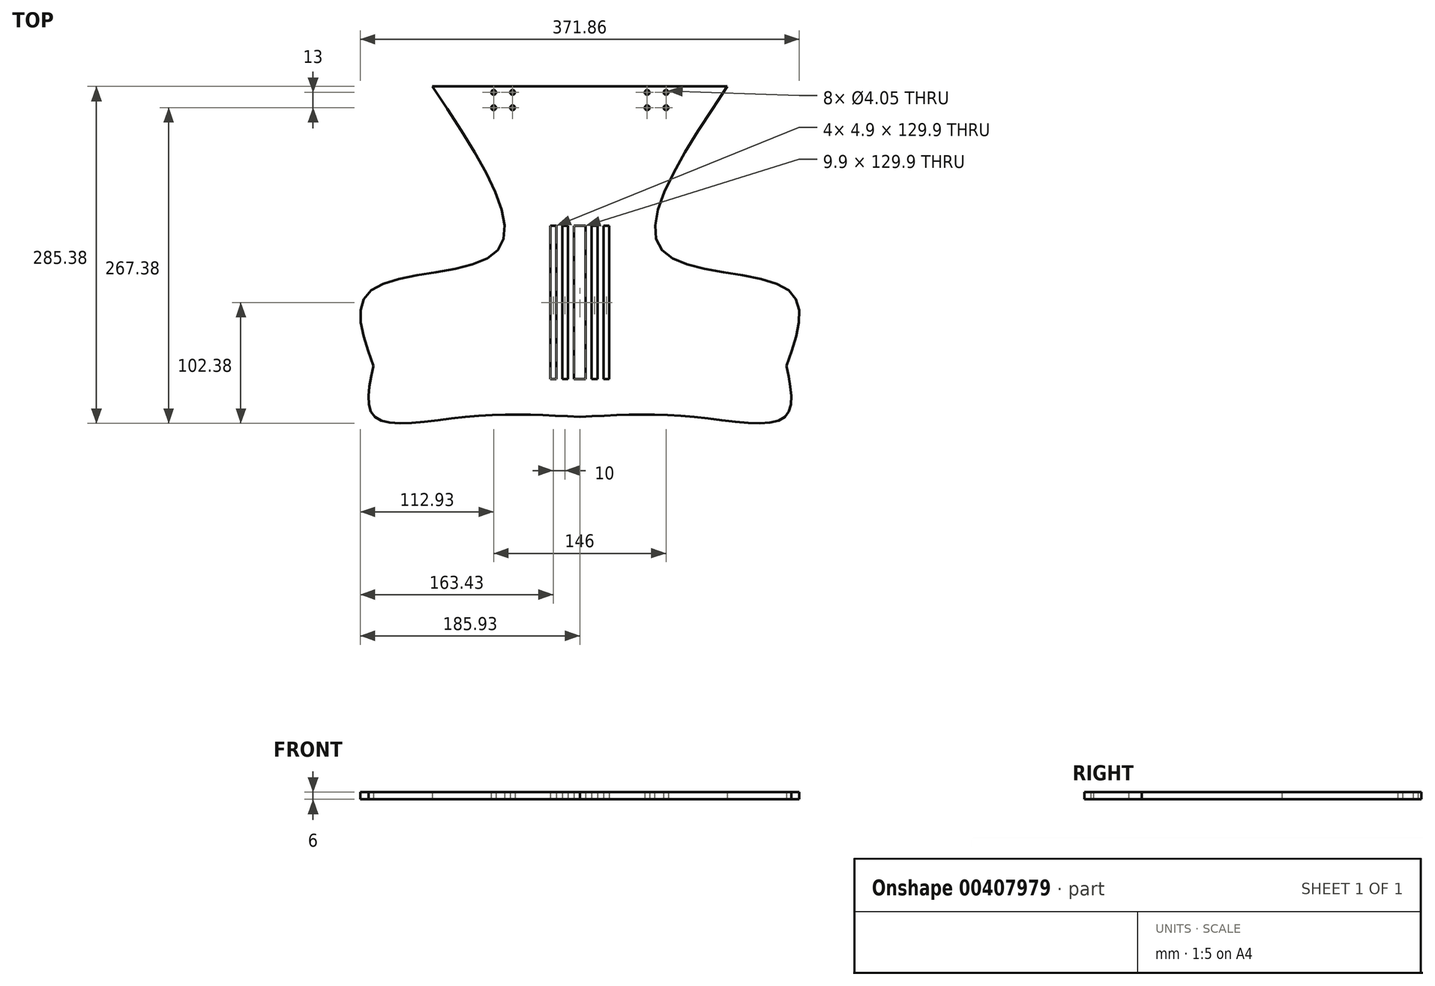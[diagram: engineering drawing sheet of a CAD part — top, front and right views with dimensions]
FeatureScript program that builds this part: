
annotation { "Feature Type Name" : "Feature", "Feature Type Description" : "" }
export const myFeature = defineFeature(function(context is Context, id is Id, definition is map)
    precondition{}
    {
        {
            var Q0;
            Q0=qCreatedBy(makeId("Top.planeOp"),FACE);
            var sketch = newSketch(context, id + "F0", { "sketchPlane" : qUnion([Q0])});
            skLineSegment(sketch, "E0.bottom", {"start": v(-125, 0) * mm, "end": v(125, 0) * mm, "construction": true});
            skLineSegment(sketch, "E0.top", {"start": v(-125, -280) * mm, "end": v(125, -280) * mm, "construction": true});
            skLineSegment(sketch, "E0.left", {"start": v(-125, 0) * mm, "end": v(-125, -280) * mm, "construction": true});
            skLineSegment(sketch, "E0.right", {"start": v(125, 0) * mm, "end": v(125, -280) * mm, "construction": true});
            skFitSpline(sketch, "E1", {"points": [v(-125, 0) * mm, v(-175, -236.88) * mm], "startDerivative": vector(163.58, -419.06) * mm, "endDerivative": vector(5.98, -192.46) * mm});
            skPoint(sketch, "E2", {"position": v(0, -280) * mm});
            skFitSpline(sketch, "E3", {"points": [v(-175, -236.88) * mm, v(0, -280) * mm], "startDerivative": vector(4.02, -129.37) * mm, "endDerivative": vector(290.73, 0) * mm});
            skFitSpline(sketch, "E4.MirrorCS", {"points": [v(125, 0) * mm, v(175, -236.88) * mm], "startDerivative": vector(-163.58, -419.06) * mm, "endDerivative": vector(-5.98, -192.46) * mm});
            skFitSpline(sketch, "E5.MirrorCS", {"points": [v(175, -236.88) * mm, v(0, -280) * mm], "startDerivative": vector(-4.02, -129.37) * mm, "endDerivative": vector(-290.73, 0) * mm});
            skFitSpline(sketch, "E6", {"points": [v(-125, 0) * mm, v(0, 25) * mm], "startDerivative": vector(-31, 79.42) * mm, "endDerivative": vector(148.36, 0.98) * mm});
            skFitSpline(sketch, "E7.MirrorCS", {"points": [v(125, 0) * mm, v(0, 25) * mm], "startDerivative": vector(31, 79.42) * mm, "endDerivative": vector(-148.36, 0.98) * mm});
            skLineSegment(sketch, "E8.bottom", {"start": v(-10, -88) * mm, "end": v(-5, -88) * mm, "construction": true});
            skLineSegment(sketch, "E8.top", {"start": v(-10, -278) * mm, "end": v(-5, -278) * mm, "construction": true});
            skLineSegment(sketch, "E8.left", {"start": v(-10, -88) * mm, "end": v(-10, -278) * mm, "construction": true});
            skLineSegment(sketch, "E8.right", {"start": v(-5, -88) * mm, "end": v(-5, -278) * mm, "construction": true});
            skLineSegment(sketch, "E9.1.0.0", {"start": v(-20, -88) * mm, "end": v(-20, -278) * mm, "construction": true});
            skLineSegment(sketch, "E9.1.0.1", {"start": v(-15, -88) * mm, "end": v(-15, -278) * mm, "construction": true});
            skLineSegment(sketch, "E9.1.0.2", {"start": v(-20, -88) * mm, "end": v(-15, -88) * mm, "construction": true});
            skLineSegment(sketch, "E9.1.0.3", {"start": v(-20, -278) * mm, "end": v(-15, -278) * mm, "construction": true});
            skLineSegment(sketch, "E9.2.0.0", {"start": v(-30, -88) * mm, "end": v(-30, -278) * mm, "construction": true});
            skLineSegment(sketch, "E9.2.0.1", {"start": v(-25, -88) * mm, "end": v(-25, -278) * mm, "construction": true});
            skLineSegment(sketch, "E9.2.0.2", {"start": v(-30, -88) * mm, "end": v(-25, -88) * mm, "construction": true});
            skLineSegment(sketch, "E9.2.0.3", {"start": v(-30, -278) * mm, "end": v(-25, -278) * mm, "construction": true});
            skLineSegment(sketch, "E9.direction1", {"start": v(-10, -278) * mm, "end": v(-20, -278) * mm, "construction": true});
            skLineSegment(sketch, "E10.MirrorCS", {"start": v(10, -278) * mm, "end": v(20, -278) * mm, "construction": true});
            skLineSegment(sketch, "E11.MirrorCS", {"start": v(20, -278) * mm, "end": v(15, -278) * mm, "construction": true});
            skLineSegment(sketch, "E12.MirrorCS", {"start": v(10, -278) * mm, "end": v(5, -278) * mm, "construction": true});
            skLineSegment(sketch, "E13.MirrorCS", {"start": v(20, -88) * mm, "end": v(15, -88) * mm, "construction": true});
            skLineSegment(sketch, "E14.MirrorCS", {"start": v(30, -278) * mm, "end": v(25, -278) * mm, "construction": true});
            skLineSegment(sketch, "E15.MirrorCS", {"start": v(10, -88) * mm, "end": v(5, -88) * mm, "construction": true});
            skLineSegment(sketch, "E16.MirrorCS", {"start": v(30, -88) * mm, "end": v(25, -88) * mm, "construction": true});
            skLineSegment(sketch, "E17.MirrorCS", {"start": v(30, -88) * mm, "end": v(30, -278) * mm, "construction": true});
            skLineSegment(sketch, "E18.MirrorCS", {"start": v(10, -88) * mm, "end": v(10, -278) * mm, "construction": true});
            skLineSegment(sketch, "E19.MirrorCS", {"start": v(15, -88) * mm, "end": v(15, -278) * mm, "construction": true});
            skLineSegment(sketch, "E20.MirrorCS", {"start": v(5, -88) * mm, "end": v(5, -278) * mm, "construction": true});
            skLineSegment(sketch, "E21.MirrorCS", {"start": v(20, -88) * mm, "end": v(20, -278) * mm, "construction": true});
            skLineSegment(sketch, "E22.MirrorCS", {"start": v(25, -88) * mm, "end": v(25, -278) * mm, "construction": true});
            skLineSegment(sketch, "E23.bottom", {"start": v(-73, -5) * mm, "end": v(-57, -5) * mm, "construction": true});
            skLineSegment(sketch, "E23.top", {"start": v(-73, -18) * mm, "end": v(-57, -18) * mm, "construction": true});
            skLineSegment(sketch, "E23.left", {"start": v(-73, -5) * mm, "end": v(-73, -18) * mm, "construction": true});
            skLineSegment(sketch, "E23.right", {"start": v(-57, -5) * mm, "end": v(-57, -18) * mm, "construction": true});
            skCircle(sketch, "E24", {"center": v(-73, -5) * mm, "radius": 2.02 * mm, "construction": true});
            skCircle(sketch, "E25", {"center": v(-57, -5) * mm, "radius": 2.02 * mm, "construction": true});
            skCircle(sketch, "E26", {"center": v(-57, -18) * mm, "radius": 2.02 * mm, "construction": true});
            skCircle(sketch, "E27", {"center": v(-73, -18) * mm, "radius": 2.02 * mm, "construction": true});
            skPoint(sketch, "E28", {"position": v(-65, -5) * mm});
            skLineSegment(sketch, "E29.MirrorCS", {"start": v(73, -18) * mm, "end": v(57, -18) * mm, "construction": true});
            skCircle(sketch, "E30.MirrorC", {"center": v(57, -5) * mm, "radius": 2.02 * mm, "construction": true});
            skCircle(sketch, "E31.MirrorC", {"center": v(57, -18) * mm, "radius": 2.02 * mm, "construction": true});
            skPoint(sketch, "E32.MirrorP", {"position": v(65, -5) * mm});
            skCircle(sketch, "E33.MirrorC", {"center": v(73, -5) * mm, "radius": 2.02 * mm, "construction": true});
            skLineSegment(sketch, "E34.MirrorCS", {"start": v(73, -5) * mm, "end": v(57, -5) * mm, "construction": true});
            skLineSegment(sketch, "E35.MirrorCS", {"start": v(57, -5) * mm, "end": v(57, -18) * mm, "construction": true});
            skCircle(sketch, "E36.MirrorC", {"center": v(73, -18) * mm, "radius": 2.02 * mm, "construction": true});
            skLineSegment(sketch, "E37.MirrorCS", {"start": v(73, -5) * mm, "end": v(73, -18) * mm, "construction": true});
            skSolve(sketch);
        }
        {
            var Q0;
            Q0=qCreatedBy(makeId("Top.planeOp"),FACE);
            var sketch = newSketch(context, id + "F1", { "sketchPlane" : qUnion([Q0])});
            skFitSpline(sketch, "E38.0", {"points": [v(-125, 0) * mm, v(-70.47, -139.69) * mm, v(-177, -172.72) * mm, v(-175, -236.88) * mm]});
            skFitSpline(sketch, "E38.1", {"points": [v(-175, -236.88) * mm, v(-173.66, -280) * mm, v(-96.91, -280) * mm, v(0, -280) * mm]});
            skFitSpline(sketch, "E38.2", {"points": [v(175, -236.88) * mm, v(173.66, -280) * mm, v(96.91, -280) * mm, v(0, -280) * mm]});
            skFitSpline(sketch, "E38.3", {"points": [v(125, 0) * mm, v(70.47, -139.69) * mm, v(177, -172.72) * mm, v(175, -236.88) * mm]});
            skLineSegment(sketch, "E38.4", {"start": v(-125, 0) * mm, "end": v(125, 0) * mm});
            skLineSegment(sketch, "E39.bottom", {"start": v(-30, -248) * mm, "end": v(-25, -248) * mm, "construction": true});
            skLineSegment(sketch, "E39.top", {"start": v(-30, -118) * mm, "end": v(-25, -118) * mm, "construction": true});
            skLineSegment(sketch, "E39.left", {"start": v(-30, -248) * mm, "end": v(-30, -118) * mm, "construction": true});
            skLineSegment(sketch, "E39.right", {"start": v(-25, -248) * mm, "end": v(-25, -118) * mm, "construction": true});
            skLineSegment(sketch, "E40.bottom", {"start": v(-20, -118) * mm, "end": v(-15, -118) * mm, "construction": true});
            skLineSegment(sketch, "E40.top", {"start": v(-20, -248) * mm, "end": v(-15, -248) * mm, "construction": true});
            skLineSegment(sketch, "E40.left", {"start": v(-20, -118) * mm, "end": v(-20, -248) * mm, "construction": true});
            skLineSegment(sketch, "E40.right", {"start": v(-15, -118) * mm, "end": v(-15, -248) * mm, "construction": true});
            skLineSegment(sketch, "E41.bottom", {"start": v(-10, -248) * mm, "end": v(-5, -248) * mm, "construction": true});
            skLineSegment(sketch, "E41.top", {"start": v(-10, -118) * mm, "end": v(-5, -118) * mm, "construction": true});
            skLineSegment(sketch, "E41.left", {"start": v(-10, -248) * mm, "end": v(-10, -118) * mm, "construction": true});
            skLineSegment(sketch, "E41.right", {"start": v(-5, -248) * mm, "end": v(-5, -118) * mm, "construction": true});
            skLineSegment(sketch, "E42.bottom", {"start": v(5, -118) * mm, "end": v(10, -118) * mm, "construction": true});
            skLineSegment(sketch, "E42.top", {"start": v(5, -248) * mm, "end": v(10, -248) * mm, "construction": true});
            skLineSegment(sketch, "E42.left", {"start": v(5, -118) * mm, "end": v(5, -248) * mm, "construction": true});
            skLineSegment(sketch, "E42.right", {"start": v(10, -118) * mm, "end": v(10, -248) * mm, "construction": true});
            skLineSegment(sketch, "E43.bottom", {"start": v(15, -248) * mm, "end": v(20, -248) * mm, "construction": true});
            skLineSegment(sketch, "E43.top", {"start": v(15, -118) * mm, "end": v(20, -118) * mm, "construction": true});
            skLineSegment(sketch, "E43.left", {"start": v(15, -248) * mm, "end": v(15, -118) * mm, "construction": true});
            skLineSegment(sketch, "E43.right", {"start": v(20, -248) * mm, "end": v(20, -118) * mm, "construction": true});
            skLineSegment(sketch, "E44.bottom", {"start": v(25, -118) * mm, "end": v(30, -118) * mm, "construction": true});
            skLineSegment(sketch, "E44.top", {"start": v(25, -248) * mm, "end": v(30, -248) * mm, "construction": true});
            skLineSegment(sketch, "E44.left", {"start": v(25, -118) * mm, "end": v(25, -248) * mm, "construction": true});
            skLineSegment(sketch, "E44.right", {"start": v(30, -118) * mm, "end": v(30, -248) * mm, "construction": true});
            skPoint(sketch, "E45", {"position": v(-30, -183) * mm});
            skLineSegment(sketch, "E46.bottom", {"start": v(-25, -118) * mm, "end": v(-20, -118) * mm, "construction": true});
            skLineSegment(sketch, "E46.top", {"start": v(-25, -248) * mm, "end": v(-20, -248) * mm, "construction": true});
            skLineSegment(sketch, "E46.left", {"start": v(-25, -118) * mm, "end": v(-25, -248) * mm, "construction": true});
            skLineSegment(sketch, "E47.bottom", {"start": v(-15, -248) * mm, "end": v(-10, -248) * mm, "construction": true});
            skLineSegment(sketch, "E47.top", {"start": v(-15, -118) * mm, "end": v(-10, -118) * mm, "construction": true});
            skLineSegment(sketch, "E47.left", {"start": v(-15, -248) * mm, "end": v(-15, -118) * mm, "construction": true});
            skLineSegment(sketch, "E48.bottom", {"start": v(-5, -118) * mm, "end": v(5, -118) * mm, "construction": true});
            skLineSegment(sketch, "E48.top", {"start": v(-5, -248) * mm, "end": v(5, -248) * mm, "construction": true});
            skLineSegment(sketch, "E48.left", {"start": v(-5, -118) * mm, "end": v(-5, -248) * mm, "construction": true});
            skLineSegment(sketch, "E49.bottom", {"start": v(10, -248) * mm, "end": v(15, -248) * mm, "construction": true});
            skLineSegment(sketch, "E49.top", {"start": v(10, -118) * mm, "end": v(15, -118) * mm, "construction": true});
            skLineSegment(sketch, "E49.left", {"start": v(10, -248) * mm, "end": v(10, -118) * mm, "construction": true});
            skLineSegment(sketch, "E50.bottom", {"start": v(20, -118) * mm, "end": v(25, -118) * mm, "construction": true});
            skLineSegment(sketch, "E50.top", {"start": v(20, -248) * mm, "end": v(25, -248) * mm, "construction": true});
            skLineSegment(sketch, "E50.left", {"start": v(20, -118) * mm, "end": v(20, -248) * mm, "construction": true});
            skLineSegment(sketch, "E51.0", {"start": v(-24.95, -118.05) * mm, "end": v(-20.05, -118.05) * mm});
            skLineSegment(sketch, "E51.1", {"start": v(-24.95, -118.05) * mm, "end": v(-24.95, -247.95) * mm});
            skLineSegment(sketch, "E51.2", {"start": v(-24.95, -247.95) * mm, "end": v(-20.05, -247.95) * mm});
            skLineSegment(sketch, "E51.3", {"start": v(-20.05, -118.05) * mm, "end": v(-20.05, -247.95) * mm});
            skLineSegment(sketch, "E52.0", {"start": v(-14.95, -118.05) * mm, "end": v(-10.05, -118.05) * mm});
            skLineSegment(sketch, "E52.1", {"start": v(-14.95, -247.95) * mm, "end": v(-14.95, -118.05) * mm});
            skLineSegment(sketch, "E52.2", {"start": v(-14.95, -247.95) * mm, "end": v(-10.05, -247.95) * mm});
            skLineSegment(sketch, "E52.3", {"start": v(-10.05, -247.95) * mm, "end": v(-10.05, -118.05) * mm});
            skLineSegment(sketch, "E53.0", {"start": v(-4.95, -118.05) * mm, "end": v(4.95, -118.05) * mm});
            skLineSegment(sketch, "E53.1", {"start": v(-4.95, -118.05) * mm, "end": v(-4.95, -247.95) * mm});
            skLineSegment(sketch, "E53.2", {"start": v(-4.95, -247.95) * mm, "end": v(4.95, -247.95) * mm});
            skLineSegment(sketch, "E53.3", {"start": v(4.95, -118.05) * mm, "end": v(4.95, -247.95) * mm});
            skLineSegment(sketch, "E54.0", {"start": v(10.05, -247.95) * mm, "end": v(10.05, -118.05) * mm});
            skLineSegment(sketch, "E54.1", {"start": v(10.05, -247.95) * mm, "end": v(14.95, -247.95) * mm});
            skLineSegment(sketch, "E54.2", {"start": v(14.95, -247.95) * mm, "end": v(14.95, -118.05) * mm});
            skLineSegment(sketch, "E54.3", {"start": v(10.05, -118.05) * mm, "end": v(14.95, -118.05) * mm});
            skLineSegment(sketch, "E55.0", {"start": v(20.05, -118.05) * mm, "end": v(24.95, -118.05) * mm});
            skLineSegment(sketch, "E55.1", {"start": v(20.05, -118.05) * mm, "end": v(20.05, -247.95) * mm});
            skLineSegment(sketch, "E55.2", {"start": v(20.05, -247.95) * mm, "end": v(24.95, -247.95) * mm});
            skLineSegment(sketch, "E55.3", {"start": v(24.95, -118.05) * mm, "end": v(24.95, -247.95) * mm});
            skCircle(sketch, "E56.0", {"center": v(-57, -18) * mm, "radius": 2.02 * mm});
            skCircle(sketch, "E56.1", {"center": v(-73, -18) * mm, "radius": 2.02 * mm});
            skCircle(sketch, "E56.2", {"center": v(-73, -5) * mm, "radius": 2.02 * mm});
            skCircle(sketch, "E56.3", {"center": v(-57, -5) * mm, "radius": 2.02 * mm});
            skCircle(sketch, "E56.4", {"center": v(57, -18) * mm, "radius": 2.02 * mm});
            skCircle(sketch, "E56.5", {"center": v(57, -5) * mm, "radius": 2.02 * mm});
            skCircle(sketch, "E56.6", {"center": v(73, -5) * mm, "radius": 2.02 * mm});
            skCircle(sketch, "E56.7", {"center": v(73, -18) * mm, "radius": 2.02 * mm});
            skSolve(sketch);
        }
        {
            var Q0;
            Q0=makeQuery(id+"F1.imprint","IMPRINT",FACE,{"disambiguationData":[TD([[makeQuery(id+"F1.imprint","IMPRINT",EDGE,{"derivedFrom":sQuery(id+"F1.wireOp",EDGE,"E38.0")}),1.0]])]});
            extrude(context, id + "F2", {"entities" : qUnion([Q0]), "depth" : 6 * mm});
        }
    });
